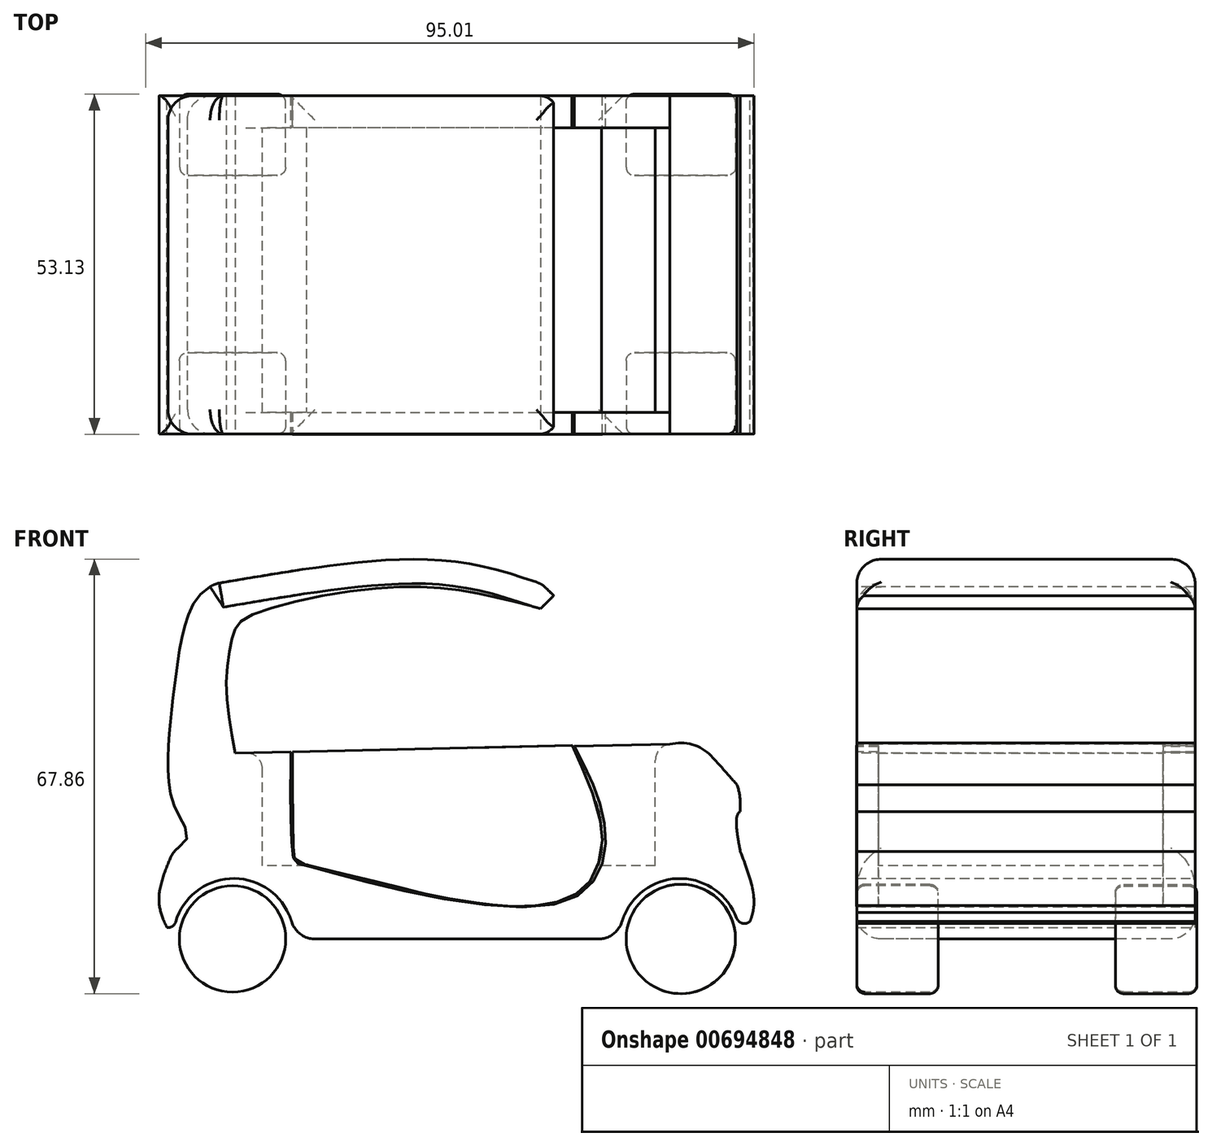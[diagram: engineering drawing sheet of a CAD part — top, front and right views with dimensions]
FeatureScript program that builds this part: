
annotation { "Feature Type Name" : "Feature", "Feature Type Description" : "" }
export const myFeature = defineFeature(function(context is Context, id is Id, definition is map)
    precondition{}
    {
        {
            var Q0;
            Q0=qCreatedBy(makeId("Front.planeOp"),FACE);
            var sketch = newSketch(context, id + "F0", { "sketchPlane" : qUnion([Q0])});
            skLineSegment(sketch, "E0", {"start": v(-24.35, 0) * mm, "end": v(26.45, 0) * mm});
            skArc(sketch, "E1", {"start": v(-24.35, 0) * mm, "mid": v(-33.27, 9.43) * mm, "end": v(-43.17, 1.04) * mm});
            skArc(sketch, "E2", {"start": v(45.26, 1.2) * mm, "mid": v(35.29, 9.42) * mm, "end": v(26.45, 0) * mm});
            skFitSpline(sketch, "E3", {"points": [v(45.33, 0) * mm, v(47.45, 5.22) * mm, v(45.33, 13.67) * mm], "startDerivative": vector(6.66, 10.93) * mm, "endDerivative": vector(-6.2, 16.22) * mm});
            skFitSpline(sketch, "E4", {"points": [v(-43.23, 13.67) * mm, v(-41, 16.11) * mm, v(-43.23, 21.22) * mm, v(-43.23, 37.9) * mm, v(-40.12, 52.34) * mm, v(-36.78, 55.45) * mm], "startDerivative": vector(25.04, 17.65) * mm, "endDerivative": vector(24.1, 15) * mm});
            skFitSpline(sketch, "E5", {"points": [v(-36.78, 55.45) * mm, v(-2.33, 59.23) * mm, v(14.34, 55.45) * mm], "startDerivative": vector(64, 11.01) * mm, "endDerivative": vector(36.64, -12.37) * mm});
            skFitSpline(sketch, "E6", {"points": [v(14.34, 55.45) * mm, v(37.23, 32.34) * mm, v(47.45, 19.9) * mm, v(45.33, 19.9) * mm, v(45.33, 13.67) * mm], "startDerivative": vector(54.24, -53.7) * mm, "endDerivative": vector(8.81, -47) * mm});
            skFitSpline(sketch, "E7", {"points": [v(44.8, 16.53) * mm, v(44.8, 24.1) * mm, v(37.23, 32.34) * mm], "startDerivative": vector(3.11, 17.17) * mm, "endDerivative": vector(-17.58, 14.54) * mm});
            skFitSpline(sketch, "E8", {"points": [v(-44.8, 3.07) * mm, v(-44.3, 1.89) * mm, v(-43.17, 1.04) * mm], "startDerivative": vector(0.71, -2.62) * mm, "endDerivative": vector(2.52, -1.46) * mm});
            skFitSpline(sketch, "E9.trimOffspring", {"points": [v(-43.23, 0) * mm, v(-45.45, 5.89) * mm, v(-43.23, 13.67) * mm], "startDerivative": vector(-6.83, 12.08) * mm, "endDerivative": vector(6.55, 15.2) * mm});
            skFitSpline(sketch, "E10", {"points": [v(47.45, 5.22) * mm, v(46.83, 2.76) * mm, v(45.26, 1.2) * mm], "startDerivative": vector(-0.7, -5.14) * mm, "endDerivative": vector(-3.73, -2.87) * mm});
            skSolve(sketch);
        }
        {
            var Q0;
            Q0=makeQuery(id+"F0.imprint","IMPRINT",FACE,{"disambiguationData":[TD([[makeQuery(id+"F0.imprint","IMPRINT",EDGE,{"derivedFrom":sQuery(id+"F0.wireOp",EDGE,"E0")}),1.0]])]});
            extrude(context, id + "F1", {"entities" : qUnion([Q0]), "depth" : 52.83 * mm, "offsetDistance" : 25.4 * mm});
        }
        {
            var Q0;
            Q0=makeQuery(id+"F1.opExtrude","SWEPT_FACE",FACE,{"disambiguationData":[OSD([sQuery(id+"F0.wireOp",EDGE,"E5")])]});
            fillet(context, id + "F2", {"entities" : qUnion([Q0]), "radius" : 3.8 * mm, "tangentPropagation" : true, "allowEdgeOverflow" : false});
        }
        {
            var Q0;
            Q0=makeQuery(id+"F1.opExtrude","CAP_FACE",FACE,{"disambiguationData":[OSD([sQuery(id+"F0.wireOp",EDGE,"E0"),sQuery(id+"F0.wireOp",EDGE,"E1"),sQuery(id+"F0.wireOp",EDGE,"E2"),sQuery(id+"F0.wireOp",EDGE,"2810468c-0104-4c3a-93ea-65795b76ce9d"),sQuery(id+"F0.wireOp",EDGE,"E3"),sQuery(id+"F0.wireOp",EDGE,"E4"),sQuery(id+"F0.wireOp",EDGE,"E5"),sQuery(id+"F0.wireOp",EDGE,"E6")])],"isStart":false});
            cPlane(context, id + "F3", {"entities" : qUnion([Q0]), "cplaneType" : CPlaneType.OFFSET, "offset" : 0 * mm, "width" : 152.4 * mm, "height" : 152.4 * mm});
        }
        {
            var Q0;
            Q0=qCreatedBy(id+"F3.planeOp",FACE);
            var sketch = newSketch(context, id + "F4", { "sketchPlane" : qUnion([Q0])});
            skCircle(sketch, "E11", {"center": v(-33.97, 0) * mm, "radius": 8.3 * mm});
            skCircle(sketch, "E12", {"center": v(36.04, 0) * mm, "radius": 8.54 * mm});
            skSolve(sketch);
        }
        {
            var Q0;
            Q0=makeQuery(id+"F4.imprint","IMPRINT",FACE,{"disambiguationData":[TD([[makeQuery(id+"F4.imprint","IMPRINT",EDGE,{"derivedFrom":sQuery(id+"F4.wireOp",EDGE,"E11")}),1.0]])]});
            var Q1;
            Q1=makeQuery(id+"F4.imprint","IMPRINT",FACE,{"disambiguationData":[TD([[makeQuery(id+"F4.imprint","IMPRINT",EDGE,{"derivedFrom":sQuery(id+"F4.wireOp",EDGE,"E12")}),1.0]])]});
            extrude(context, id + "F5", {"entities" : qUnion([Q0, Q1]), "oppositeDirection" : true, "depth" : 12.7 * mm, "offsetDistance" : 25.4 * mm});
        }
        {
            var Q0;
            Q0=makeQuery(id+"F1.opExtrude","CAP_FACE",FACE,{"disambiguationData":[OSD([sQuery(id+"F0.wireOp",EDGE,"E0"),sQuery(id+"F0.wireOp",EDGE,"E1"),sQuery(id+"F0.wireOp",EDGE,"E2"),sQuery(id+"F0.wireOp",EDGE,"2810468c-0104-4c3a-93ea-65795b76ce9d"),sQuery(id+"F0.wireOp",EDGE,"E3"),sQuery(id+"F0.wireOp",EDGE,"E4"),sQuery(id+"F0.wireOp",EDGE,"E5"),sQuery(id+"F0.wireOp",EDGE,"E6")])],"isStart":true});
            cPlane(context, id + "F6", {"entities" : qUnion([Q0]), "cplaneType" : CPlaneType.OFFSET, "offset" : 0.25 * mm, "width" : 152.4 * mm, "height" : 152.4 * mm});
        }
        {
            var Q0;
            Q0=qCreatedBy(id+"F6.planeOp",FACE);
            var sketch = newSketch(context, id + "F7", { "sketchPlane" : qUnion([Q0])});
            skCircle(sketch, "E13", {"center": v(-36.04, 0) * mm, "radius": 8.54 * mm});
            skCircle(sketch, "E14", {"center": v(33.95, 0) * mm, "radius": 8.27 * mm});
            skSolve(sketch);
        }
        {
            var Q0;
            Q0=makeQuery(id+"F7.imprint","IMPRINT",FACE,{"disambiguationData":[TD([[makeQuery(id+"F7.imprint","IMPRINT",EDGE,{"derivedFrom":sQuery(id+"F7.wireOp",EDGE,"E13")}),1.0]])]});
            var Q1;
            Q1=makeQuery(id+"F7.imprint","IMPRINT",FACE,{"disambiguationData":[TD([[makeQuery(id+"F7.imprint","IMPRINT",EDGE,{"derivedFrom":sQuery(id+"F7.wireOp",EDGE,"E14")}),1.0]])]});
            extrude(context, id + "F8", {"entities" : qUnion([Q0, Q1]), "oppositeDirection" : true, "depth" : 12.7 * mm, "offsetDistance" : 25.4 * mm});
        }
        {
            var Q0;
            Q0=makeQuery(id+"F1.opExtrude","SWEPT_FACE",FACE,{"disambiguationData":[OSD([sQuery(id+"F0.wireOp",EDGE,"E4")])]});
            var Q1;
            Q1=makeQuery(id+"F1.opExtrude","SWEPT_FACE",FACE,{"disambiguationData":[OSD([sQuery(id+"F0.wireOp",EDGE,"E0")])]});
            fillet(context, id + "F9", {"entities" : qUnion([Q0, Q1]), "radius" : 3.8 * mm, "tangentPropagation" : true, "allowEdgeOverflow" : false});
        }
        {
            var Q0;
            Q0=makeQuery(id+"F5.opExtrude","CAP_FACE",FACE,{"disambiguationData":[OSD([sQuery(id+"F4.wireOp",EDGE,"E11")])],"isStart":true});
            var Q1;
            Q1=makeQuery(id+"F5.opExtrude","CAP_EDGE",EDGE,{"disambiguationData":[OSD([sQuery(id+"F4.wireOp",EDGE,"E11")])],"isStart":false});
            var Q2;
            Q2=makeQuery(id+"F8.opExtrude","CAP_EDGE",EDGE,{"disambiguationData":[OSD([sQuery(id+"F7.wireOp",EDGE,"E14")])],"isStart":false});
            var Q3;
            Q3=makeQuery(id+"F8.opExtrude","CAP_EDGE",EDGE,{"disambiguationData":[OSD([sQuery(id+"F7.wireOp",EDGE,"E13")])],"isStart":false});
            var Q4;
            Q4=makeQuery(id+"F5.opExtrude","CAP_EDGE",EDGE,{"disambiguationData":[OSD([sQuery(id+"F4.wireOp",EDGE,"E12")])],"isStart":true});
            var Q5;
            Q5=makeQuery(id+"F5.opExtrude","CAP_EDGE",EDGE,{"disambiguationData":[OSD([sQuery(id+"F4.wireOp",EDGE,"E12")])],"isStart":false});
            var Q6;
            Q6=makeQuery(id+"F8.opExtrude","CAP_EDGE",EDGE,{"disambiguationData":[OSD([sQuery(id+"F7.wireOp",EDGE,"E13")])],"isStart":true});
            var Q7;
            Q7=makeQuery(id+"F8.opExtrude","CAP_EDGE",EDGE,{"disambiguationData":[OSD([sQuery(id+"F7.wireOp",EDGE,"E14")])],"isStart":true});
            var Q8;
            Q8=makeQuery(id+"F1.opExtrude","SWEPT_EDGE",EDGE,{"disambiguationData":[OSD([sQuery(id+"F0.wireOp",EDGE,"E1"),sQuery(id+"F0.wireOp",EDGE,"E8")])]});
            var Q9;
            Q9=makeQuery(id+"F1.opExtrude","SWEPT_EDGE",EDGE,{"disambiguationData":[OSD([sQuery(id+"F0.wireOp",EDGE,"E2"),sQuery(id+"F0.wireOp",EDGE,"E10")])]});
            fillet(context, id + "F10", {"entities" : qUnion([Q0, Q1, Q2, Q3, Q4, Q5, Q6, Q7, Q8, Q9]), "radius" : 1.27 * mm, "tangentPropagation" : true, "allowEdgeOverflow" : false});
        }
        {
            var Q0;
            Q0=makeQuery(id+"F1.opExtrude","CAP_FACE",FACE,{"disambiguationData":[OSD([sQuery(id+"F0.wireOp",EDGE,"E0"),sQuery(id+"F0.wireOp",EDGE,"E1"),sQuery(id+"F0.wireOp",EDGE,"E2"),sQuery(id+"F0.wireOp",EDGE,"E3"),sQuery(id+"F0.wireOp",EDGE,"E4"),sQuery(id+"F0.wireOp",EDGE,"E5"),sQuery(id+"F0.wireOp",EDGE,"E6"),sQuery(id+"F0.wireOp",EDGE,"E7"),sQuery(id+"F0.wireOp",EDGE,"E6"),sQuery(id+"F0.wireOp",EDGE,"E8"),sQuery(id+"F0.wireOp",EDGE,"E9.trimOffspring"),sQuery(id+"F0.wireOp",EDGE,"E10")])],"isStart":false});
            cPlane(context, id + "F11", {"entities" : qUnion([Q0]), "cplaneType" : CPlaneType.OFFSET, "offset" : 0 * mm, "width" : 152.4 * mm, "height" : 152.4 * mm});
        }
        {
            var Q0;
            Q0=qCreatedBy(id+"F11.planeOp",FACE);
            var sketch = newSketch(context, id + "F12", { "sketchPlane" : qUnion([Q0])});
            skLineSegment(sketch, "E15", {"start": v(34.35, 30.4) * mm, "end": v(14.16, 51.6) * mm});
            skFitSpline(sketch, "E16", {"points": [v(14.16, 51.6) * mm, v(2.67, 54.27) * mm, v(-12.57, 54.67) * mm, v(-32.08, 50.01) * mm, v(-33.96, 47.24) * mm, v(-34.95, 40.01) * mm, v(-33.56, 29.02) * mm], "startDerivative": vector(-65.12, 17.33) * mm, "endDerivative": vector(12.56, -66.6) * mm});
            skLineSegment(sketch, "E17", {"start": v(-33.56, 29.02) * mm, "end": v(34.35, 30.4) * mm});
            skSolve(sketch);
        }
        {
            var Q0;
            Q0=makeQuery(id+"F12.imprint","IMPRINT",FACE,{"disambiguationData":[TD([[makeQuery(id+"F12.imprint","IMPRINT",EDGE,{"derivedFrom":sQuery(id+"F12.wireOp",EDGE,"E15")}),1.0]])]});
            extrude(context, id + "F13", {"entities" : qUnion([Q0]), "operationType" : NewBodyOperationType.REMOVE, "oppositeDirection" : true, "depth" : 72.14 * mm, "offsetDistance" : 25.4 * mm});
        }
        {
            var Q0;
            Q0=qCreatedBy(makeId("Top.planeOp"),FACE);
            cPlane(context, id + "F14", {"entities" : qUnion([Q0]), "cplaneType" : CPlaneType.OFFSET, "offset" : 30.73 * mm, "width" : 152.4 * mm, "height" : 152.4 * mm});
        }
        {
            var Q0;
            Q0=qCreatedBy(id+"F14.planeOp",FACE);
            var sketch = newSketch(context, id + "F15", { "sketchPlane" : qUnion([Q0])});
            skLineSegment(sketch, "E18.bottom", {"start": v(32.07, -49.46) * mm, "end": v(-29.29, -49.46) * mm});
            skLineSegment(sketch, "E18.top", {"start": v(32.07, -5.03) * mm, "end": v(-29.29, -5.03) * mm});
            skLineSegment(sketch, "E18.left", {"start": v(32.07, -49.46) * mm, "end": v(32.07, -5.03) * mm});
            skLineSegment(sketch, "E18.right", {"start": v(-29.29, -49.46) * mm, "end": v(-29.29, -5.03) * mm});
            skSolve(sketch);
        }
        {
            var Q0;
            Q0=makeQuery(id+"F15.imprint","IMPRINT",FACE,{"disambiguationData":[TD([[makeQuery(id+"F15.imprint","IMPRINT",EDGE,{"derivedFrom":sQuery(id+"F15.wireOp",EDGE,"E18.bottom")}),-1.0]])]});
            extrude(context, id + "F16", {"entities" : qUnion([Q0]), "operationType" : NewBodyOperationType.REMOVE, "oppositeDirection" : true, "depth" : 19.3 * mm, "offsetDistance" : 25.4 * mm});
        }
        {
            var Q0;
            Q0=makeQuery(id+"F16.boolean.opBoolean","INTERSECT",EDGE,{"derivedFrom":[makeQuery(id+"F13.boolean.opBoolean","COPY",FACE,{"derivedFrom":makeQuery(id+"F13.opExtrude","SWEPT_FACE",FACE,{"disambiguationData":[OSD([sQuery(id+"F12.wireOp",EDGE,"E17")])]})}),makeQuery(id+"F16.opExtrude","SWEPT_FACE",FACE,{"disambiguationData":[OSD([sQuery(id+"F15.wireOp",EDGE,"E18.right")])]})]});
            var Q1;
            Q1=makeQuery(id+"F16.boolean.opBoolean","INTERSECT",EDGE,{"derivedFrom":[makeQuery(id+"F13.boolean.opBoolean","COPY",FACE,{"derivedFrom":makeQuery(id+"F13.opExtrude","SWEPT_FACE",FACE,{"disambiguationData":[OSD([sQuery(id+"F12.wireOp",EDGE,"E17")])]})}),makeQuery(id+"F16.opExtrude","SWEPT_FACE",FACE,{"disambiguationData":[OSD([sQuery(id+"F15.wireOp",EDGE,"E18.left")])]})]});
            fillet(context, id + "F17", {"entities" : qUnion([Q0, Q1]), "radius" : 2.54 * mm, "tangentPropagation" : true, "allowEdgeOverflow" : false});
        }
        {
            var Q0;
            Q0=qCreatedBy(makeId("Right.planeOp"),FACE);
            var Q1;
            {var subQ0=sQuery(id+"F0.wireOp",EDGE,"E6");Q1=makeQuery(id+"F2.opFillet","BLEND_EDGE",EDGE,{"blendedFrom":[makeQuery(id+"F1.opExtrude","SWEPT_EDGE",EDGE,{"disambiguationData":[OSD([sQuery(id+"F0.wireOp",EDGE,"E5"),subQ0])]}),makeQuery(id+"F1.opExtrude","SWEPT_FACE",FACE,{"disambiguationData":[OSD([subQ0])]})],"blendedInto":[makeQuery(id+"F1.opExtrude","SWEPT_FACE",FACE,{"disambiguationData":[OSD([subQ0])]})]});}
            cPlane(context, id + "F18", {"entities" : qUnion([Q0, Q1]), "cplaneType" : CPlaneType.LINE_ANGLE, "offset" : 15.24 * mm, "angle" : 45 * degree, "oppositeDirection" : true, "width" : 152.4 * mm, "height" : 152.4 * mm});
        }
        {
            var Q0;
            Q0=qCreatedBy(id+"F18.planeOp",FACE);
            var sketch = newSketch(context, id + "F19", { "sketchPlane" : qUnion([Q0])});
            skLineSegment(sketch, "E19.bottom", {"start": v(50, 26.1) * mm, "end": v(2.73, 26.1) * mm});
            skLineSegment(sketch, "E19.top", {"start": v(50, 0) * mm, "end": v(2.73, 0) * mm});
            skLineSegment(sketch, "E19.left", {"start": v(50, 26.1) * mm, "end": v(50, 0) * mm});
            skLineSegment(sketch, "E19.right", {"start": v(2.73, 26.1) * mm, "end": v(2.73, 0) * mm});
            skSolve(sketch);
        }
        {
            var Q0;
            Q0=makeQuery(id+"F19.imprint","IMPRINT",FACE,{"disambiguationData":[TD([[makeQuery(id+"F19.imprint","IMPRINT",EDGE,{"derivedFrom":sQuery(id+"F19.wireOp",EDGE,"E19.bottom")}),1.0]])]});
            var Q1;
            Q1=makeQuery(id+"F13.boolean.opBoolean","COPY",FACE,{"derivedFrom":makeQuery(id+"F13.opExtrude","SWEPT_FACE",FACE,{"disambiguationData":[OSD([sQuery(id+"F12.wireOp",EDGE,"E15")])]})});
            extrude(context, id + "F20", {"entities" : qUnion([Q0, Q1]), "operationType" : NewBodyOperationType.REMOVE, "oppositeDirection" : true, "depth" : 26.67 * mm, "offsetDistance" : 25.4 * mm});
        }
        {
            var Q0;
            Q0=makeQuery(id+"F20.boolean.opBoolean","INTERSECT",EDGE,{"derivedFrom":[makeQuery(id+"F1.opExtrude","SWEPT_FACE",FACE,{"disambiguationData":[OSD([sQuery(id+"F0.wireOp",EDGE,"E6")])]}),makeQuery(id+"F20.opExtrude","SWEPT_FACE",FACE,{"disambiguationData":[OSD([sQuery(id+"F12.wireOp",EDGE,"E15"),sQuery(id+"F12.wireOp",EDGE,"E17"),sQuery(id+"F15.wireOp",EDGE,"E18.left")])]})]});
            fillet(context, id + "F21", {"entities" : qUnion([Q0]), "radius" : 6.5 * mm, "tangentPropagation" : true, "allowEdgeOverflow" : false});
        }
        {
            var Q0;
            Q0=makeQuery(id+"F1.opExtrude","CAP_FACE",FACE,{"disambiguationData":[OSD([sQuery(id+"F0.wireOp",EDGE,"E0"),sQuery(id+"F0.wireOp",EDGE,"E1"),sQuery(id+"F0.wireOp",EDGE,"E2"),sQuery(id+"F0.wireOp",EDGE,"E3"),sQuery(id+"F0.wireOp",EDGE,"E4"),sQuery(id+"F0.wireOp",EDGE,"E5"),sQuery(id+"F0.wireOp",EDGE,"E6"),sQuery(id+"F0.wireOp",EDGE,"E7"),sQuery(id+"F0.wireOp",EDGE,"E6"),sQuery(id+"F0.wireOp",EDGE,"E8"),sQuery(id+"F0.wireOp",EDGE,"E9.trimOffspring"),sQuery(id+"F0.wireOp",EDGE,"E10")])],"isStart":false});
            cPlane(context, id + "F22", {"entities" : qUnion([Q0]), "cplaneType" : CPlaneType.OFFSET, "offset" : 0 * mm, "width" : 152.4 * mm, "height" : 152.4 * mm});
        }
        {
            var Q0;
            Q0=qCreatedBy(id+"F22.planeOp",FACE);
            var sketch = newSketch(context, id + "F23", { "sketchPlane" : qUnion([Q0])});
            skFitSpline(sketch, "E20", {"points": [v(19.45, 30.04) * mm, v(24.28, 16.47) * mm, v(17.08, 5.58) * mm, v(-22.48, 11.43) * mm, v(-24.54, 13.08) * mm, v(-24.85, 29.21) * mm, v(-24.76, 29.95) * mm, v(-24.15, 31.35) * mm], "startDerivative": vector(38.73, -74.9) * mm, "endDerivative": vector(13.16, 29.08) * mm});
            skFitSpline(sketch, "E21", {"points": [v(19.45, 30.04) * mm, v(19.3, 30.19) * mm], "startDerivative": vector(-0.14, 0.15) * mm, "endDerivative": vector(-0.14, 0.15) * mm});
            skLineSegment(sketch, "E22", {"start": v(19.3, 30.19) * mm, "end": v(-24.85, 29.21) * mm});
            skSolve(sketch);
        }
        {
            var Q0;
            Q0=makeQuery(id+"F23.imprint","IMPRINT",FACE,{"disambiguationData":[TD([[makeQuery(id+"F23.imprint","IMPRINT",EDGE,{"derivedFrom":sQuery(id+"F23.wireOp",EDGE,"E20")}),-1.0]])]});
            extrude(context, id + "F24", {"entities" : qUnion([Q0]), "operationType" : NewBodyOperationType.REMOVE, "oppositeDirection" : true, "depth" : 84.07 * mm, "offsetDistance" : 25.4 * mm});
        }
        {
            var Q0;
            Q0=makeQuery(id+"F1.opExtrude","CAP_FACE",FACE,{"disambiguationData":[OSD([sQuery(id+"F0.wireOp",EDGE,"E0"),sQuery(id+"F0.wireOp",EDGE,"E1"),sQuery(id+"F0.wireOp",EDGE,"E2"),sQuery(id+"F0.wireOp",EDGE,"E3"),sQuery(id+"F0.wireOp",EDGE,"E4"),sQuery(id+"F0.wireOp",EDGE,"E5"),sQuery(id+"F0.wireOp",EDGE,"E6"),sQuery(id+"F0.wireOp",EDGE,"E7"),sQuery(id+"F0.wireOp",EDGE,"E6"),sQuery(id+"F0.wireOp",EDGE,"E8"),sQuery(id+"F0.wireOp",EDGE,"E9.trimOffspring"),sQuery(id+"F0.wireOp",EDGE,"E10")])],"isStart":true});
            cPlane(context, id + "F25", {"entities" : qUnion([Q0]), "cplaneType" : CPlaneType.OFFSET, "offset" : 0 * mm, "width" : 152.4 * mm, "height" : 152.4 * mm});
        }
        {
            var Q0;
            Q0=qCreatedBy(id+"F25.planeOp",FACE);
            var sketch = newSketch(context, id + "F26", { "sketchPlane" : qUnion([Q0])});
            skFitSpline(sketch, "E23", {"points": [v(-19.05, 30.23) * mm, v(-22.07, 23.23) * mm, v(-23.54, 18.01) * mm, v(-23.54, 13.32) * mm, v(-22.39, 9.87) * mm, v(-20.2, 7.37) * mm, v(-16.12, 5.6) * mm, v(-12.84, 5.17) * mm, v(-9.68, 5.1) * mm, v(-5.33, 5.44) * mm, v(-1.55, 6.01) * mm, v(1.47, 6.5) * mm, v(4.57, 7.21) * mm, v(9, 8.18) * mm, v(11.84, 8.84) * mm, v(18.44, 10.5) * mm, v(21.83, 11.42) * mm, v(23.48, 11.9) * mm, v(24.06, 12.13) * mm, v(24.37, 12.94) * mm, v(24.51, 14.82) * mm, v(24.6, 20.5) * mm, v(24.63, 27.06) * mm, v(24.6, 29.2) * mm], "startDerivative": vector(-51.78, -113.61) * mm, "endDerivative": vector(-0.67, 54.25) * mm});
            skLineSegment(sketch, "E24", {"start": v(-19.05, 30.23) * mm, "end": v(24.6, 29.2) * mm});
            skSolve(sketch);
        }
        {
            var Q0;
            Q0=makeQuery(id+"F26.imprint","IMPRINT",FACE,{"disambiguationData":[TD([[makeQuery(id+"F26.imprint","IMPRINT",EDGE,{"derivedFrom":sQuery(id+"F26.wireOp",EDGE,"E23")}),1.0]])]});
            extrude(context, id + "F27", {"entities" : qUnion([Q0]), "oppositeDirection" : true, "depth" : 5 * mm, "offsetDistance" : 25.4 * mm});
        }
        {
            var Q0;
            Q0=makeQuery(id+"F26.imprint","IMPRINT",FACE,{"disambiguationData":[TD([[makeQuery(id+"F26.imprint","IMPRINT",EDGE,{"derivedFrom":sQuery(id+"F26.wireOp",EDGE,"E23")}),1.0]])]});
            cPlane(context, id + "F28", {"entities" : qUnion([Q0]), "cplaneType" : CPlaneType.OFFSET, "offset" : 52.88 * mm, "oppositeDirection" : true, "width" : 152.4 * mm, "height" : 152.4 * mm});
        }
        {
            var Q0;
            Q0=qCreatedBy(id+"F28.planeOp",FACE);
            var sketch = newSketch(context, id + "F29", { "sketchPlane" : qUnion([Q0])});
            skFitSpline(sketch, "E25", {"points": [v(24.6, 29.21) * mm, v(24.58, 21.07) * mm, v(24.5, 14.86) * mm, v(24.44, 13.38) * mm, v(24.31, 12.68) * mm, v(24.13, 12.2) * mm, v(23.8, 11.98) * mm, v(15.3, 9.88) * mm, v(9.38, 8.42) * mm, v(5.04, 7.35) * mm, v(3.27, 6.93) * mm, v(-3.1, 5.79) * mm, v(-5.55, 5.47) * mm, v(-7.42, 5.23) * mm, v(-10.54, 5.1) * mm, v(-14.5, 5.32) * mm, v(-17.26, 5.92) * mm, v(-19.96, 7.2) * mm, v(-21.74, 8.85) * mm, v(-22.96, 11.1) * mm, v(-23.72, 14.89) * mm, v(-23.67, 16.91) * mm, v(-22.73, 21.39) * mm, v(-20.55, 26.89) * mm, v(-19.07, 30.22) * mm], "startDerivative": vector(-0.2, -123.08) * mm, "endDerivative": vector(31.52, 70.5) * mm});
            skLineSegment(sketch, "E26", {"start": v(24.6, 29.21) * mm, "end": v(-19.07, 30.22) * mm});
            skSolve(sketch);
        }
        {
            var Q0;
            Q0=makeQuery(id+"F29.imprint","IMPRINT",FACE,{"disambiguationData":[TD([[makeQuery(id+"F29.imprint","IMPRINT",EDGE,{"derivedFrom":sQuery(id+"F29.wireOp",EDGE,"E25")}),-1.0]])]});
            extrude(context, id + "F30", {"entities" : qUnion([Q0]), "depth" : 3.45 * mm, "offsetDistance" : 25.4 * mm});
        }
    });
